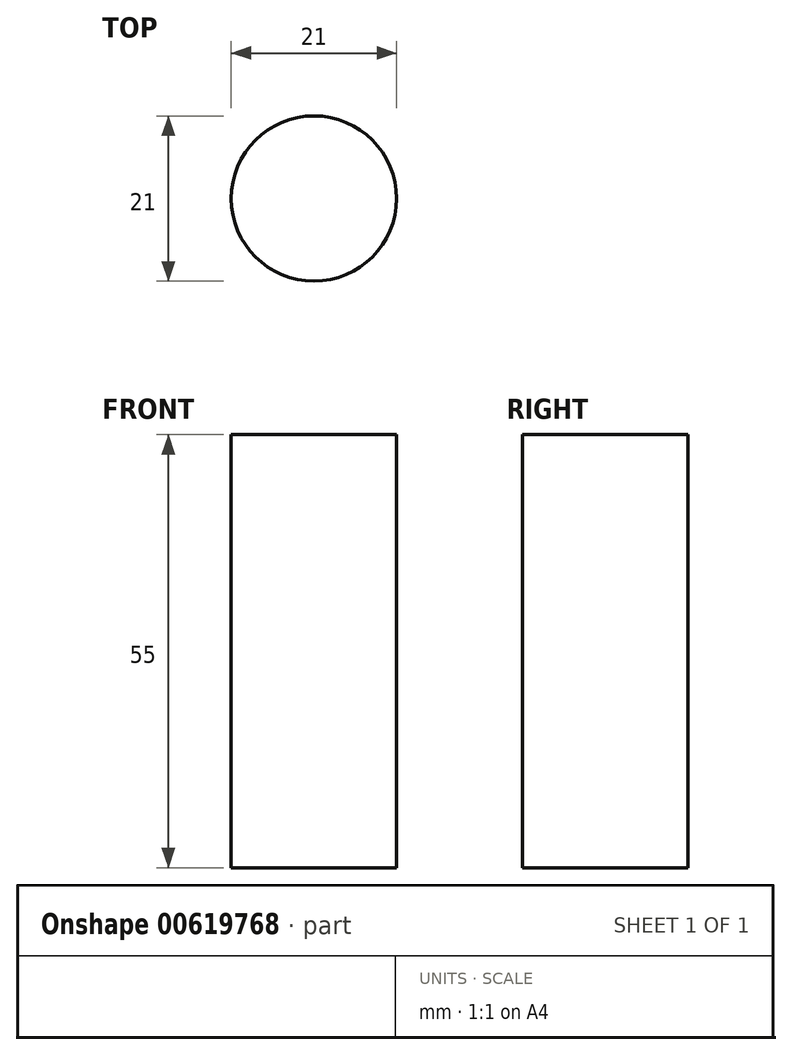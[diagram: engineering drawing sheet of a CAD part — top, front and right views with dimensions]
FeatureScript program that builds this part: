
annotation { "Feature Type Name" : "Feature", "Feature Type Description" : "" }
export const myFeature = defineFeature(function(context is Context, id is Id, definition is map)
    precondition{}
    {
        {
            var Q0;
            Q0=qCreatedBy(makeId("Top.planeOp"),FACE);
            var sketch = newSketch(context, id + "F0", { "sketchPlane" : qUnion([Q0])});
            skCircle(sketch, "E0", {"center": v(0, 0) * mm, "radius": 10.5 * mm});
            skSolve(sketch);
        }
        {
            var Q0;
            Q0=makeQuery(id+"F0.imprint","IMPRINT",FACE,{"disambiguationData":[TD([[makeQuery(id+"F0.imprint","IMPRINT",EDGE,{"derivedFrom":sQuery(id+"F0.wireOp",EDGE,"E0")}),1.0]])]});
            extrude(context, id + "F1", {"entities" : qUnion([Q0]), "depth" : 55 * mm, "offsetDistance" : 25 * mm});
        }
    });
